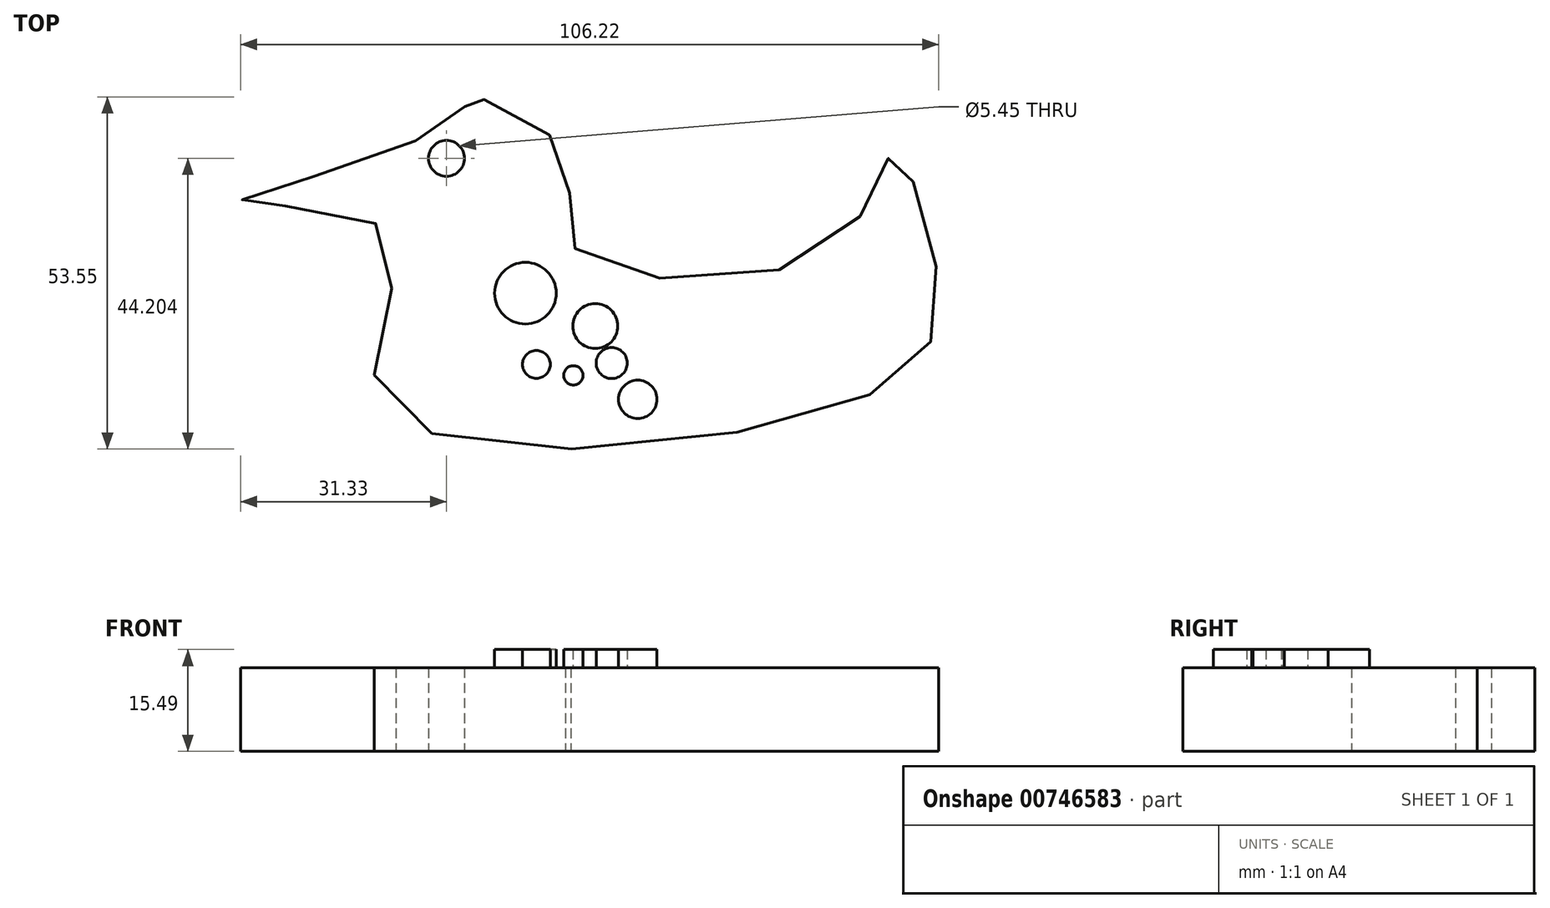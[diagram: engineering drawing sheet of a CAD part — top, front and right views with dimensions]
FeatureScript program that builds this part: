
annotation { "Feature Type Name" : "Feature", "Feature Type Description" : "" }
export const myFeature = defineFeature(function(context is Context, id is Id, definition is map)
    precondition{}
    {
        {
            var Q0;
            Q0=qCreatedBy(makeId("Top.planeOp"),FACE);
            var sketch = newSketch(context, id + "F0", { "sketchPlane" : qUnion([Q0])});
            skFitSpline(sketch, "E0", {"points": [v(-39.7, 39.3) * mm, v(-31.58, 45.59) * mm, v(-31.17, 46) * mm, v(-16.75, 37.06) * mm, v(-15.94, 23.45) * mm, v(23.86, 23.45) * mm, v(33, 37.26) * mm, v(39.7, 18.17) * mm, v(27.72, 0) * mm, v(-44.98, 0) * mm, v(-43.96, 25.28) * mm, v(-66.3, 29.95) * mm, v(-39.7, 39.3) * mm]});
            skSolve(sketch);
        }
        {
            var Q0;
            Q0=makeQuery(id+"F0.imprint","IMPRINT",FACE,{"disambiguationData":[TD([[makeQuery(id+"F0.imprint","IMPRINT",EDGE,{"derivedFrom":sQuery(id+"F0.wireOp",EDGE,"E0")}),-1.0]])]});
            extrude(context, id + "F1", {"entities" : qUnion([Q0]), "depth" : 12.7 * mm, "offsetDistance" : 25.4 * mm});
        }
        {
            var Q0;
            Q0=qCreatedBy(makeId("Top.planeOp"),FACE);
            var sketch = newSketch(context, id + "F2", { "sketchPlane" : qUnion([Q0])});
            skCircle(sketch, "E1", {"center": v(-35.03, 36.65) * mm, "radius": 2.72 * mm});
            skSolve(sketch);
        }
        {
            var Q0;
            Q0 = qSketchRegion(id + "F2", true);
            extrude(context, id + "F3", {"entities" : qUnion([Q0]), "operationType" : NewBodyOperationType.REMOVE, "depth" : 48.5 * mm, "offsetDistance" : 25.4 * mm});
        }
        {
            var Q0;
            Q0=qCreatedBy(makeId("Top.planeOp"),FACE);
            var sketch = newSketch(context, id + "F4", { "sketchPlane" : qUnion([Q0])});
            skCircle(sketch, "E2", {"center": v(-23.02, 16.15) * mm, "radius": 4.68 * mm});
            skCircle(sketch, "E3", {"center": v(-12.4, 11.15) * mm, "radius": 3.42 * mm});
            skCircle(sketch, "E4", {"center": v(-21.36, 5.31) * mm, "radius": 2.12 * mm});
            skCircle(sketch, "E5", {"center": v(-15.73, 3.65) * mm, "radius": 1.47 * mm});
            skCircle(sketch, "E6", {"center": v(-9.9, 5.52) * mm, "radius": 2.36 * mm});
            skCircle(sketch, "E7", {"center": v(-5.94, 0) * mm, "radius": 2.92 * mm});
            skSolve(sketch);
        }
        {
            var Q0;
            Q0=makeQuery(id+"F4.imprint","IMPRINT",FACE,{"disambiguationData":[TD([[makeQuery(id+"F4.imprint","IMPRINT",EDGE,{"derivedFrom":sQuery(id+"F4.wireOp",EDGE,"E7")}),1.0]])]});
            var Q1;
            Q1=makeQuery(id+"F4.imprint","IMPRINT",FACE,{"disambiguationData":[TD([[makeQuery(id+"F4.imprint","IMPRINT",EDGE,{"derivedFrom":sQuery(id+"F4.wireOp",EDGE,"E2")}),1.0]])]});
            var Q2;
            Q2=makeQuery(id+"F4.imprint","IMPRINT",FACE,{"disambiguationData":[TD([[makeQuery(id+"F4.imprint","IMPRINT",EDGE,{"derivedFrom":sQuery(id+"F4.wireOp",EDGE,"E4")}),1.0]])]});
            var Q3;
            Q3=makeQuery(id+"F4.imprint","IMPRINT",FACE,{"disambiguationData":[TD([[makeQuery(id+"F4.imprint","IMPRINT",EDGE,{"derivedFrom":sQuery(id+"F4.wireOp",EDGE,"E5")}),1.0]])]});
            var Q4;
            Q4=makeQuery(id+"F4.imprint","IMPRINT",FACE,{"disambiguationData":[TD([[makeQuery(id+"F4.imprint","IMPRINT",EDGE,{"derivedFrom":sQuery(id+"F4.wireOp",EDGE,"E3")}),1.0]])]});
            var Q5;
            Q5=makeQuery(id+"F4.imprint","IMPRINT",FACE,{"disambiguationData":[TD([[makeQuery(id+"F4.imprint","IMPRINT",EDGE,{"derivedFrom":sQuery(id+"F4.wireOp",EDGE,"E6")}),1.0]])]});
            extrude(context, id + "F5", {"entities" : qUnion([Q0, Q1, Q2, Q3, Q4, Q5]), "operationType" : NewBodyOperationType.ADD, "depth" : 15.5 * mm, "offsetDistance" : 25.4 * mm});
        }
    });
